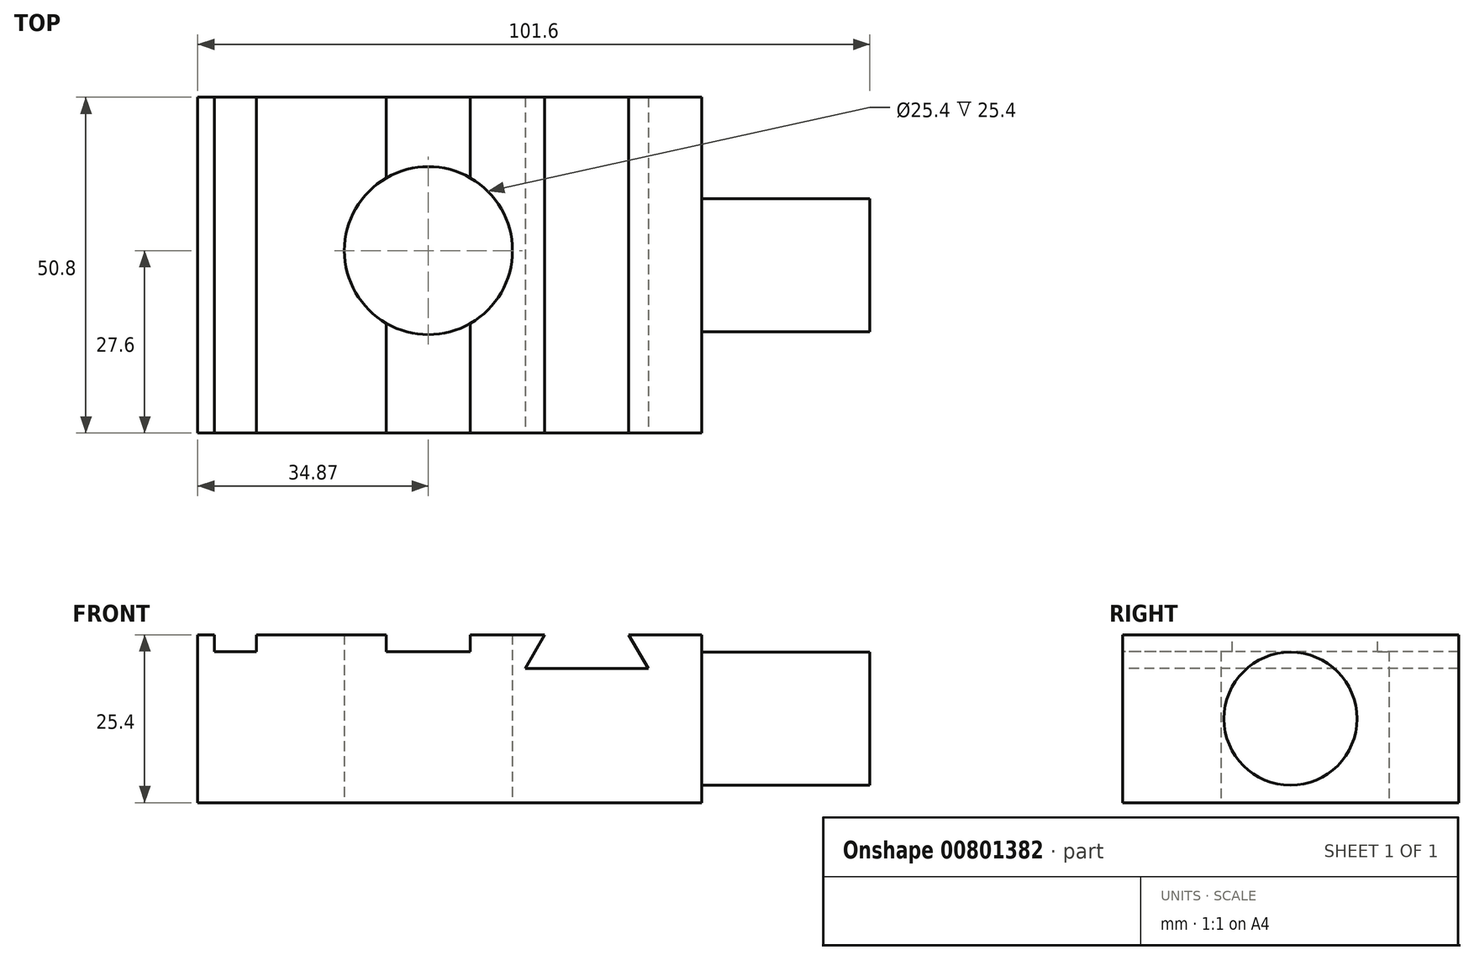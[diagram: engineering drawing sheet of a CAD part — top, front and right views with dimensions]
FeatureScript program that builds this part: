
annotation { "Feature Type Name" : "Feature", "Feature Type Description" : "" }
export const myFeature = defineFeature(function(context is Context, id is Id, definition is map)
    precondition{}
    {
        {
            var Q0;
            Q0=qCreatedBy(makeId("Top.planeOp"),FACE);
            var sketch = newSketch(context, id + "F0", { "sketchPlane" : qUnion([Q0])});
            skLineSegment(sketch, "E0.bottom", {"start": v(-34.87, 23.2) * mm, "end": v(41.33, 23.2) * mm});
            skLineSegment(sketch, "E0.top", {"start": v(-34.87, -27.6) * mm, "end": v(41.33, -27.6) * mm});
            skLineSegment(sketch, "E0.left", {"start": v(-34.87, 23.2) * mm, "end": v(-34.87, -27.6) * mm});
            skLineSegment(sketch, "E0.right", {"start": v(41.33, 23.2) * mm, "end": v(41.33, -27.6) * mm});
            skCircle(sketch, "E1", {"center": v(0, 0) * mm, "radius": 12.7 * mm});
            skSolve(sketch);
        }
        {
            var Q0;
            Q0=makeQuery(id+"F0.imprint","IMPRINT",FACE,{"disambiguationData":[TD([[makeQuery(id+"F0.imprint","IMPRINT",EDGE,{"derivedFrom":sQuery(id+"F0.wireOp",EDGE,"E0.bottom")}),-1.0]])]});
            extrude(context, id + "F1", {"entities" : qUnion([Q0]), "depth" : 25.4 * mm, "offsetDistance" : 25.4 * mm});
        }
        {
            var Q0;
            Q0=makeQuery(id+"F1.opExtrude","CAP_FACE",FACE,{"disambiguationData":[OSD([sQuery(id+"F0.wireOp",EDGE,"E0.bottom"),sQuery(id+"F0.wireOp",EDGE,"E0.top"),sQuery(id+"F0.wireOp",EDGE,"E0.left"),sQuery(id+"F0.wireOp",EDGE,"E0.right"),sQuery(id+"F0.wireOp",EDGE,"E1")])],"isStart":false});
            var sketch = newSketch(context, id + "F2", { "sketchPlane" : qUnion([Q0])});
            skLineSegment(sketch, "E2.bottom", {"start": v(-32.33, 23.2) * mm, "end": v(-25.98, 23.2) * mm});
            skLineSegment(sketch, "E2.top", {"start": v(-32.33, -27.6) * mm, "end": v(-25.98, -27.6) * mm});
            skLineSegment(sketch, "E2.left", {"start": v(-32.33, 23.2) * mm, "end": v(-32.33, -27.6) * mm});
            skLineSegment(sketch, "E2.right", {"start": v(-25.98, 23.2) * mm, "end": v(-25.98, -27.6) * mm});
            skLineSegment(sketch, "E3", {"start": v(-6.35, 23.2) * mm, "end": v(-6.35, -27.6) * mm});
            skLineSegment(sketch, "E4", {"start": v(-6.35, -27.6) * mm, "end": v(6.35, -27.6) * mm});
            skLineSegment(sketch, "E5", {"start": v(6.35, -27.6) * mm, "end": v(6.35, 23.2) * mm});
            skLineSegment(sketch, "E6", {"start": v(6.35, 23.2) * mm, "end": v(-6.35, 23.2) * mm});
            skPoint(sketch, "E7", {"position": v(0, -1.82) * mm});
            skLineSegment(sketch, "E8", {"start": v(0, 23.2) * mm, "end": v(0, -27.6) * mm, "construction": true});
            skSolve(sketch);
        }
        {
            var Q0;
            Q0=makeQuery(id+"F2.imprint","IMPRINT",FACE,{"disambiguationData":[TD([[makeQuery(id+"F2.imprint","IMPRINT",EDGE,{"derivedFrom":sQuery(id+"F2.wireOp",EDGE,"E2.bottom")}),-1.0]])]});
            var Q1;
            {var subQ0=sQuery(id+"F2.wireOp",EDGE,"E4");Q1=makeQuery(id+"F2.imprint","IMPRINT",FACE,{"disambiguationData":[TD([[makeQuery(id+"F2.imprint","IMPRINT",EDGE,{"derivedFrom":subQ0}),1.0]])]});}
            var Q2;
            {var subQ0=sQuery(id+"F2.wireOp",EDGE,"E6");Q2=makeQuery(id+"F2.imprint","IMPRINT",FACE,{"disambiguationData":[TD([[makeQuery(id+"F2.imprint","IMPRINT",EDGE,{"derivedFrom":subQ0}),-1.0]])]});}
            extrude(context, id + "F3", {"entities" : qUnion([Q0, Q1, Q2]), "operationType" : NewBodyOperationType.REMOVE, "oppositeDirection" : true, "depth" : 2.54 * mm, "offsetDistance" : 25.4 * mm});
        }
        {
            var Q0;
            Q0=makeQuery(id+"F1.opExtrude","SWEPT_FACE",FACE,{"disambiguationData":[OSD([sQuery(id+"F0.wireOp",EDGE,"E0.top")])]});
            var sketch = newSketch(context, id + "F4", { "sketchPlane" : qUnion([Q0])});
            skLineSegment(sketch, "E9", {"start": v(17.59, 25.4) * mm, "end": v(14.65, 20.32) * mm});
            skLineSegment(sketch, "E10", {"start": v(14.65, 20.32) * mm, "end": v(33.22, 20.32) * mm});
            skLineSegment(sketch, "E11", {"start": v(33.22, 20.32) * mm, "end": v(30.29, 25.4) * mm});
            skLineSegment(sketch, "E12", {"start": v(30.29, 25.4) * mm, "end": v(17.59, 25.4) * mm});
            skSolve(sketch);
        }
        {
            var Q0;
            Q0=makeQuery(id+"F1.opExtrude","SWEPT_FACE",FACE,{"disambiguationData":[OSD([sQuery(id+"F0.wireOp",EDGE,"E0.right")])]});
            var sketch = newSketch(context, id + "F5", { "sketchPlane" : qUnion([Q0])});
            skCircle(sketch, "E13", {"center": v(-2.2, 12.7) * mm, "radius": 10.06 * mm});
            skPoint(sketch, "E13.centerSnap0", {"position": v(-2.2, 25.4) * mm});
            skPoint(sketch, "E13.centerSnap1", {"position": v(-27.6, 12.7) * mm});
            skSolve(sketch);
        }
        {
            var Q0;
            Q0 = qSketchRegion(id + "F5", true);
            extrude(context, id + "F6", {"entities" : qUnion([Q0]), "operationType" : NewBodyOperationType.ADD, "depth" : 25.4 * mm, "offsetDistance" : 25.4 * mm});
        }
        {
            var Q0;
            Q0 = qSketchRegion(id + "F5", true);
            extrude(context, id + "F7", {"entities" : qUnion([Q0]), "operationType" : NewBodyOperationType.ADD, "oppositeDirection" : true, "depth" : 12.45 * mm, "offsetDistance" : 25.4 * mm});
        }
        {
            var Q0;
            Q0=makeQuery(id+"F4.imprint","IMPRINT",FACE,{"disambiguationData":[TD([[makeQuery(id+"F4.imprint","IMPRINT",EDGE,{"derivedFrom":sQuery(id+"F4.wireOp",EDGE,"E9")}),1.0]])]});
            extrude(context, id + "F8", {"entities" : qUnion([Q0]), "operationType" : NewBodyOperationType.REMOVE, "oppositeDirection" : true, "depth" : 70.36 * mm, "offsetDistance" : 25.4 * mm});
        }
    });
